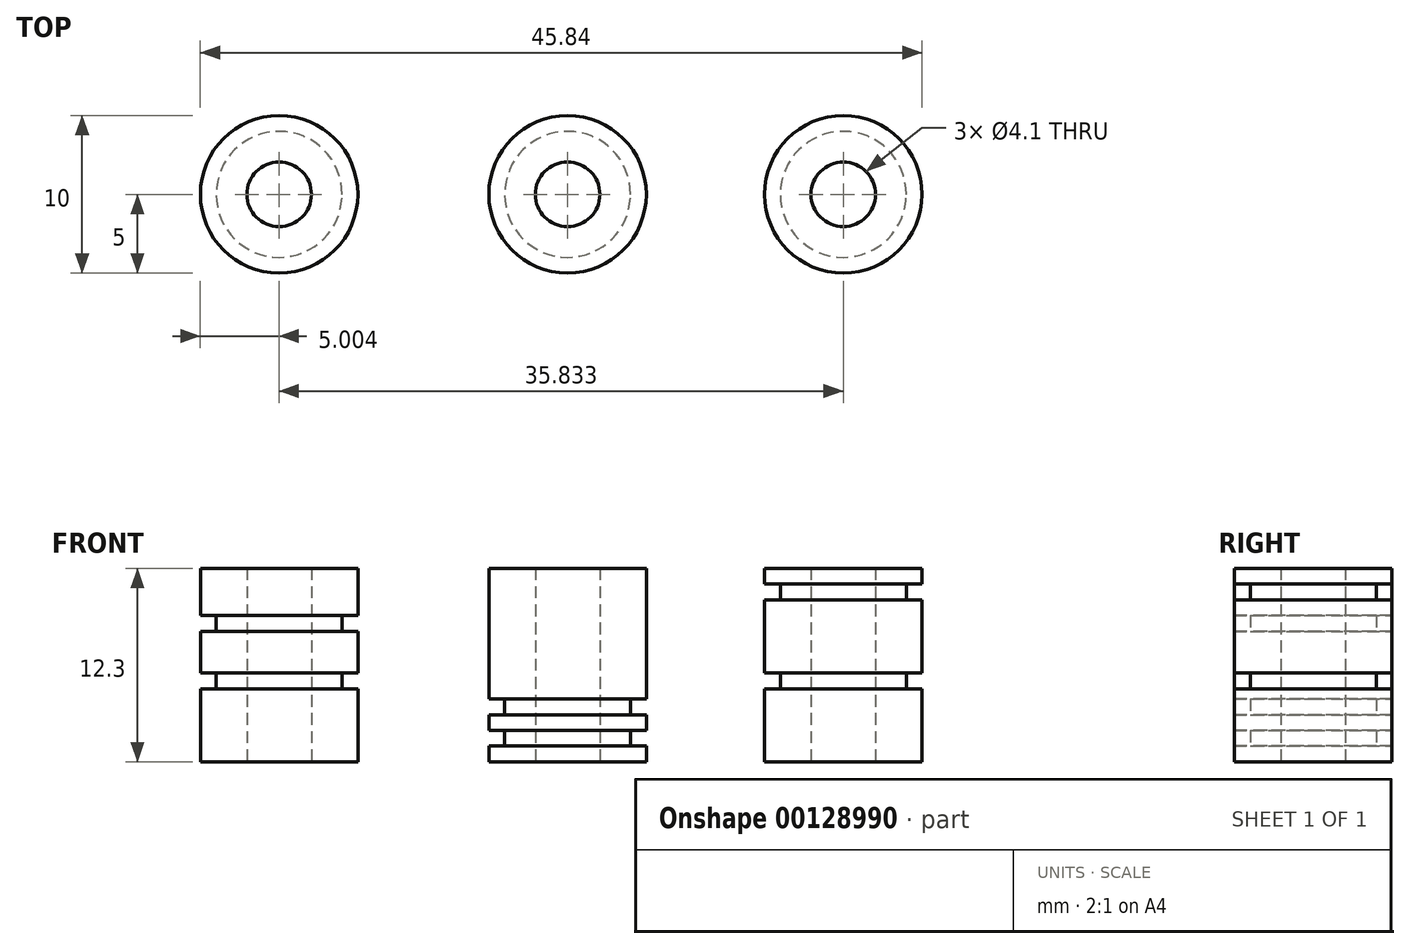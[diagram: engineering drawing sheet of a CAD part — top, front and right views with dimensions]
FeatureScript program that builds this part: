
annotation { "Feature Type Name" : "Feature", "Feature Type Description" : "" }
export const myFeature = defineFeature(function(context is Context, id is Id, definition is map)
    precondition{}
    {
        {
            var Q0;
            Q0=qCreatedBy(makeId("Top.planeOp"),FACE);
            var sketch = newSketch(context, id + "F0", { "sketchPlane" : qUnion([Q0])});
            skCircle(sketch, "E0", {"center": v(-18.12, -0.56) * mm, "radius": 2.05 * mm});
            skCircle(sketch, "E1", {"center": v(-18.12, -0.56) * mm, "radius": 5 * mm});
            skCircle(sketch, "E2", {"center": v(17.72, -0.56) * mm, "radius": 2.05 * mm});
            skCircle(sketch, "E3", {"center": v(17.72, -0.56) * mm, "radius": 5 * mm});
            skCircle(sketch, "E4", {"center": v(0.2, -0.56) * mm, "radius": 2.05 * mm});
            skCircle(sketch, "E5", {"center": v(0.2, -0.56) * mm, "radius": 5 * mm});
            skSolve(sketch);
        }
        {
            var Q0;
            Q0=makeQuery(id+"F0.imprint","IMPRINT",FACE,{"disambiguationData":[TD([[makeQuery(id+"F0.imprint","IMPRINT",EDGE,{"derivedFrom":sQuery(id+"F0.wireOp",EDGE,"E4")}),-1.0]])]});
            extrude(context, id + "F1", {"entities" : qUnion([Q0]), "depth" : 1 * mm});
        }
        {
            var Q0;
            Q0=makeQuery(id+"F1.opExtrude","CAP_FACE",FACE,{"disambiguationData":[OSD([sQuery(id+"F0.wireOp",EDGE,"E4"),sQuery(id+"F0.wireOp",EDGE,"E5")])],"isStart":false});
            var sketch = newSketch(context, id + "F2", { "sketchPlane" : qUnion([Q0])});
            skCircle(sketch, "E6", {"center": v(0.2, -0.56) * mm, "radius": 4 * mm});
            skSolve(sketch);
        }
        {
            var Q0;
            Q0=makeQuery(id+"F2.imprint","IMPRINT",FACE,{"disambiguationData":[TD([[makeQuery(id+"F2.imprint","IMPRINT",EDGE,{"derivedFrom":sQuery(id+"F2.wireOp",EDGE,"E6")}),1.0]])]});
            extrude(context, id + "F3", {"entities" : qUnion([Q0]), "operationType" : NewBodyOperationType.ADD, "depth" : 1 * mm});
        }
        {
            var Q0;
            Q0=makeQuery(id+"F3.opExtrude","CAP_FACE",FACE,{"disambiguationData":[OSD([sQuery(id+"F0.wireOp",EDGE,"E4"),sQuery(id+"F2.wireOp",EDGE,"E6")])],"isStart":false});
            var sketch = newSketch(context, id + "F4", { "sketchPlane" : qUnion([Q0])});
            skCircle(sketch, "E7", {"center": v(0.2, -0.56) * mm, "radius": 5 * mm});
            skSolve(sketch);
        }
        {
            var Q0;
            Q0=makeQuery(id+"F4.imprint","IMPRINT",FACE,{"disambiguationData":[TD([[makeQuery(id+"F4.imprint","IMPRINT",EDGE,{"derivedFrom":sQuery(id+"F4.wireOp",EDGE,"E7")}),1.0]])]});
            var Q1;
            Q1=makeQuery(id+"F4.imprint","IMPRINT",FACE,{"disambiguationData":[TD([[makeQuery(id+"F4.imprint","IMPRINT",EDGE,{"derivedFrom":makeQuery(id+"F3.opExtrude","CAP_EDGE",EDGE,{"disambiguationData":[OSD([sQuery(id+"F2.wireOp",EDGE,"E6")])],"isStart":false})}),1.0]])]});
            extrude(context, id + "F5", {"entities" : qUnion([Q0, Q1]), "operationType" : NewBodyOperationType.ADD, "depth" : 1 * mm});
        }
        {
            var Q0;
            Q0=makeQuery(id+"F5.opExtrude","CAP_FACE",FACE,{"disambiguationData":[OSD([sQuery(id+"F0.wireOp",EDGE,"E4"),sQuery(id+"F4.wireOp",EDGE,"E7")])],"isStart":false});
            var sketch = newSketch(context, id + "F6", { "sketchPlane" : qUnion([Q0])});
            skCircle(sketch, "E8", {"center": v(0.2, -0.56) * mm, "radius": 4 * mm});
            skSolve(sketch);
        }
        {
            var Q0;
            Q0=makeQuery(id+"F6.imprint","IMPRINT",FACE,{"disambiguationData":[TD([[makeQuery(id+"F6.imprint","IMPRINT",EDGE,{"derivedFrom":sQuery(id+"F6.wireOp",EDGE,"E8")}),1.0]])]});
            extrude(context, id + "F7", {"entities" : qUnion([Q0]), "operationType" : NewBodyOperationType.ADD, "depth" : 1 * mm});
        }
        {
            var Q0;
            Q0=makeQuery(id+"F7.opExtrude","CAP_FACE",FACE,{"disambiguationData":[OSD([sQuery(id+"F0.wireOp",EDGE,"E4"),sQuery(id+"F6.wireOp",EDGE,"E8")])],"isStart":false});
            var sketch = newSketch(context, id + "F8", { "sketchPlane" : qUnion([Q0])});
            skCircle(sketch, "E9", {"center": v(0.2, -0.56) * mm, "radius": 5 * mm});
            skSolve(sketch);
        }
        {
            var Q0;
            Q0=makeQuery(id+"F8.imprint","IMPRINT",FACE,{"disambiguationData":[TD([[makeQuery(id+"F8.imprint","IMPRINT",EDGE,{"derivedFrom":sQuery(id+"F8.wireOp",EDGE,"E9")}),1.0]])]});
            var Q1;
            Q1=makeQuery(id+"F8.imprint","IMPRINT",FACE,{"disambiguationData":[TD([[makeQuery(id+"F8.imprint","IMPRINT",EDGE,{"derivedFrom":makeQuery(id+"F7.opExtrude","CAP_EDGE",EDGE,{"disambiguationData":[OSD([sQuery(id+"F6.wireOp",EDGE,"E8")])],"isStart":false})}),1.0]])]});
            extrude(context, id + "F9", {"entities" : qUnion([Q0, Q1]), "operationType" : NewBodyOperationType.ADD, "depth" : 8.3 * mm});
        }
        {
            var Q0;
            Q0=makeQuery(id+"F0.imprint","IMPRINT",FACE,{"disambiguationData":[TD([[makeQuery(id+"F0.imprint","IMPRINT",EDGE,{"derivedFrom":sQuery(id+"F0.wireOp",EDGE,"E2")}),-1.0]])]});
            extrude(context, id + "F10", {"entities" : qUnion([Q0]), "depth" : 4.65 * mm});
        }
        {
            var Q0;
            Q0=makeQuery(id+"F10.opExtrude","CAP_FACE",FACE,{"disambiguationData":[OSD([sQuery(id+"F0.wireOp",EDGE,"E2"),sQuery(id+"F0.wireOp",EDGE,"E3")])],"isStart":false});
            var sketch = newSketch(context, id + "F11", { "sketchPlane" : qUnion([Q0])});
            skCircle(sketch, "E10", {"center": v(17.72, -0.56) * mm, "radius": 4 * mm});
            skSolve(sketch);
        }
        {
            var Q0;
            Q0=makeQuery(id+"F11.imprint","IMPRINT",FACE,{"disambiguationData":[TD([[makeQuery(id+"F11.imprint","IMPRINT",EDGE,{"derivedFrom":sQuery(id+"F11.wireOp",EDGE,"E10")}),1.0]])]});
            extrude(context, id + "F12", {"entities" : qUnion([Q0]), "operationType" : NewBodyOperationType.ADD, "depth" : 1 * mm});
        }
        {
            var Q0;
            Q0=makeQuery(id+"F12.opExtrude","CAP_FACE",FACE,{"disambiguationData":[OSD([sQuery(id+"F0.wireOp",EDGE,"E2"),sQuery(id+"F11.wireOp",EDGE,"E10")])],"isStart":false});
            var sketch = newSketch(context, id + "F13", { "sketchPlane" : qUnion([Q0])});
            skCircle(sketch, "E11", {"center": v(17.72, -0.56) * mm, "radius": 5 * mm});
            skSolve(sketch);
        }
        {
            var Q0;
            Q0=makeQuery(id+"F13.imprint","IMPRINT",FACE,{"disambiguationData":[TD([[makeQuery(id+"F13.imprint","IMPRINT",EDGE,{"derivedFrom":sQuery(id+"F13.wireOp",EDGE,"E11")}),1.0]])]});
            var Q1;
            Q1=makeQuery(id+"F13.imprint","IMPRINT",FACE,{"disambiguationData":[TD([[makeQuery(id+"F13.imprint","IMPRINT",EDGE,{"derivedFrom":makeQuery(id+"F12.opExtrude","CAP_EDGE",EDGE,{"disambiguationData":[OSD([sQuery(id+"F11.wireOp",EDGE,"E10")])],"isStart":false})}),1.0]])]});
            extrude(context, id + "F14", {"entities" : qUnion([Q0, Q1]), "operationType" : NewBodyOperationType.ADD, "depth" : 4.65 * mm});
        }
        {
            var Q0;
            Q0=makeQuery(id+"F0.imprint","IMPRINT",FACE,{"disambiguationData":[TD([[makeQuery(id+"F0.imprint","IMPRINT",EDGE,{"derivedFrom":sQuery(id+"F0.wireOp",EDGE,"E0")}),-1.0]])]});
            extrude(context, id + "F15", {"entities" : qUnion([Q0]), "depth" : 4.65 * mm});
        }
        {
            var Q0;
            Q0=makeQuery(id+"F15.opExtrude","CAP_FACE",FACE,{"disambiguationData":[OSD([sQuery(id+"F0.wireOp",EDGE,"E0"),sQuery(id+"F0.wireOp",EDGE,"E1")])],"isStart":false});
            var sketch = newSketch(context, id + "F16", { "sketchPlane" : qUnion([Q0])});
            skCircle(sketch, "E12", {"center": v(-18.12, -0.56) * mm, "radius": 4 * mm});
            skSolve(sketch);
        }
        {
            var Q0;
            Q0=makeQuery(id+"F16.imprint","IMPRINT",FACE,{"disambiguationData":[TD([[makeQuery(id+"F16.imprint","IMPRINT",EDGE,{"derivedFrom":sQuery(id+"F16.wireOp",EDGE,"E12")}),1.0]])]});
            extrude(context, id + "F17", {"entities" : qUnion([Q0]), "operationType" : NewBodyOperationType.ADD, "depth" : 1 * mm});
        }
        {
            var Q0;
            Q0=makeQuery(id+"F17.opExtrude","CAP_FACE",FACE,{"disambiguationData":[OSD([sQuery(id+"F0.wireOp",EDGE,"E0"),sQuery(id+"F16.wireOp",EDGE,"E12")])],"isStart":false});
            var sketch = newSketch(context, id + "F18", { "sketchPlane" : qUnion([Q0])});
            skCircle(sketch, "E13", {"center": v(-18.12, -0.56) * mm, "radius": 5 * mm});
            skSolve(sketch);
        }
        {
            var Q0;
            Q0=makeQuery(id+"F18.imprint","IMPRINT",FACE,{"disambiguationData":[TD([[makeQuery(id+"F18.imprint","IMPRINT",EDGE,{"derivedFrom":sQuery(id+"F18.wireOp",EDGE,"E13")}),1.0]])]});
            var Q1;
            Q1=makeQuery(id+"F18.imprint","IMPRINT",FACE,{"disambiguationData":[TD([[makeQuery(id+"F18.imprint","IMPRINT",EDGE,{"derivedFrom":makeQuery(id+"F17.opExtrude","CAP_EDGE",EDGE,{"disambiguationData":[OSD([sQuery(id+"F16.wireOp",EDGE,"E12")])],"isStart":false})}),1.0]])]});
            extrude(context, id + "F19", {"entities" : qUnion([Q0, Q1]), "operationType" : NewBodyOperationType.ADD, "depth" : 2.65 * mm});
        }
        {
            var Q0;
            Q0=makeQuery(id+"F19.opExtrude","CAP_FACE",FACE,{"disambiguationData":[OSD([sQuery(id+"F0.wireOp",EDGE,"E0"),sQuery(id+"F18.wireOp",EDGE,"E13")])],"isStart":false});
            var sketch = newSketch(context, id + "F20", { "sketchPlane" : qUnion([Q0])});
            skCircle(sketch, "E14", {"center": v(-18.12, -0.56) * mm, "radius": 4 * mm});
            skSolve(sketch);
        }
        {
            var Q0;
            Q0=makeQuery(id+"F20.imprint","IMPRINT",FACE,{"disambiguationData":[TD([[makeQuery(id+"F20.imprint","IMPRINT",EDGE,{"derivedFrom":sQuery(id+"F20.wireOp",EDGE,"E14")}),1.0]])]});
            extrude(context, id + "F21", {"entities" : qUnion([Q0]), "operationType" : NewBodyOperationType.ADD, "depth" : 1 * mm});
        }
        {
            var Q0;
            Q0=makeQuery(id+"F21.opExtrude","CAP_FACE",FACE,{"disambiguationData":[OSD([sQuery(id+"F0.wireOp",EDGE,"E0"),sQuery(id+"F20.wireOp",EDGE,"E14")])],"isStart":false});
            var sketch = newSketch(context, id + "F22", { "sketchPlane" : qUnion([Q0])});
            skCircle(sketch, "E15", {"center": v(-18.12, -0.56) * mm, "radius": 5 * mm});
            skSolve(sketch);
        }
        {
            var Q0;
            Q0=makeQuery(id+"F22.imprint","IMPRINT",FACE,{"disambiguationData":[TD([[makeQuery(id+"F22.imprint","IMPRINT",EDGE,{"derivedFrom":sQuery(id+"F22.wireOp",EDGE,"E15")}),1.0]])]});
            var Q1;
            Q1=makeQuery(id+"F22.imprint","IMPRINT",FACE,{"disambiguationData":[TD([[makeQuery(id+"F22.imprint","IMPRINT",EDGE,{"derivedFrom":makeQuery(id+"F21.opExtrude","CAP_EDGE",EDGE,{"disambiguationData":[OSD([sQuery(id+"F20.wireOp",EDGE,"E14")])],"isStart":false})}),1.0]])]});
            extrude(context, id + "F23", {"entities" : qUnion([Q0, Q1]), "operationType" : NewBodyOperationType.ADD, "depth" : 3 * mm});
        }
        {
            var Q0;
            Q0=makeQuery(id+"F14.opExtrude","CAP_FACE",FACE,{"disambiguationData":[OSD([sQuery(id+"F0.wireOp",EDGE,"E2"),sQuery(id+"F13.wireOp",EDGE,"E11")])],"isStart":false});
            var sketch = newSketch(context, id + "F24", { "sketchPlane" : qUnion([Q0])});
            skCircle(sketch, "E16", {"center": v(17.72, -0.56) * mm, "radius": 4 * mm});
            skSolve(sketch);
        }
        {
            var Q0;
            Q0=makeQuery(id+"F24.imprint","IMPRINT",FACE,{"disambiguationData":[TD([[makeQuery(id+"F24.imprint","IMPRINT",EDGE,{"derivedFrom":sQuery(id+"F24.wireOp",EDGE,"E16")}),1.0]])]});
            extrude(context, id + "F25", {"entities" : qUnion([Q0]), "operationType" : NewBodyOperationType.ADD, "depth" : 1 * mm});
        }
        {
            var Q0;
            Q0=makeQuery(id+"F25.opExtrude","CAP_FACE",FACE,{"disambiguationData":[OSD([sQuery(id+"F0.wireOp",EDGE,"E2"),sQuery(id+"F24.wireOp",EDGE,"E16")])],"isStart":false});
            var sketch = newSketch(context, id + "F26", { "sketchPlane" : qUnion([Q0])});
            skCircle(sketch, "E17", {"center": v(17.72, -0.56) * mm, "radius": 5 * mm});
            skSolve(sketch);
        }
        {
            var Q0;
            Q0=makeQuery(id+"F26.imprint","IMPRINT",FACE,{"disambiguationData":[TD([[makeQuery(id+"F26.imprint","IMPRINT",EDGE,{"derivedFrom":sQuery(id+"F26.wireOp",EDGE,"E17")}),1.0]])]});
            var Q1;
            Q1=makeQuery(id+"F26.imprint","IMPRINT",FACE,{"disambiguationData":[TD([[makeQuery(id+"F26.imprint","IMPRINT",EDGE,{"derivedFrom":makeQuery(id+"F25.opExtrude","CAP_EDGE",EDGE,{"disambiguationData":[OSD([sQuery(id+"F24.wireOp",EDGE,"E16")])],"isStart":false})}),1.0]])]});
            extrude(context, id + "F27", {"entities" : qUnion([Q0, Q1]), "operationType" : NewBodyOperationType.ADD, "depth" : 1 * mm});
        }
    });
